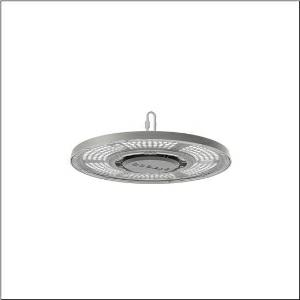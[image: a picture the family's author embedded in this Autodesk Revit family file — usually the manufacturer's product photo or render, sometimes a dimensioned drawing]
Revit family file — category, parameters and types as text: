
# Revit family: highbay_31-s_51hc42da4fmb
name_source: partatom
category: Lighting Fixtures
units: mm (PartAtom-declared; Revit-internal decimal feet)

## family parameters
Cut with Voids When Loaded = No
Host = Face
Light Source = No
Part Type = Normal
Room Calculation Point = No
Round Connector Dimension = Use Diameter
Shared = No

## types (1)
- Highbay 31-S (1 x LED, 14000 lm, 94 W, 4000K)
    Apparent Load = 94 VA
    CIE Flux Codes = 77 99 100 100 100
    Color Rendering = 80
    Color Temperature = 4000K
    Default Elevation = 1800 mm
    Description = Highbay 31-S, high bay luminaire, primary light control with lens, of PC, primary optical cover: cover panel, of PC, transparent, light emission: direct distribution, primary light characteristic: rotationally symmetric, installation type: suspended mounting, surface-mounted, LED, rated luminous flux: 14.000lm, luminous efficacy: 150lm/W, light colour: 840, colour temperature: 4000K, control gear: DALI 2, with cable, 5x 1.0mm², free wire ends, mains connection: 220..240V, AC/DC, 0/50..60Hz, cable length: 1,5m, rated input power: 94W, housing, rotationally symmetric, of diecast aluminium, powder-coated, grey aluminium (RAL 9007), with hook on luminaire side, incl. screw, diameter: 339mm, protection rating (complete): IP65, insulation class (complete): insulation class I (protective earthing), certification: CE, ENEC, UKCA, protection symbol: D, impact resistance: IK08, permissible operating ambient temperature: -30..+45°C, standard: EN 60598-2-22, EN 60598, corresponds to IFS (International Featured Standards) requirements for safety and quality in the food industry, packaging unit: 1 piece
    Height = 141 mm
    Lamp = 1 x LED
    Lamp Light Flux = 14000 lm
    Lamp Power = 94 W
    Lamp count = 1
    Length = 339 mm
    Luminous efficacy = 149 lm/W
    Manufacturer = Siteco
    ModVariant = No
    Model = 51HC42DA4FMB
    Mounting Place = Ceiling
    Mounting Type = Pendant
    Number of Poles = 1
    OnlyDefault = Yes
    Power Factor = 1
    Product Name = Highbay 31-S
    Product group = high bay luminaire
    ProductGroupID = 901
    Protection Class = Protection class I
    Protection Degree = IP 65
    RLX_Detail_Level = 1
    RLX_Emergency_Light_Flux = 0 lm
    RLX_Emergency_Type = 0
    RLX_Emergency_Type_DB = No
    RlxData = <blob elided: 162409 chars, md5=86317613>
    Socket = socket
    Standby Power = 0 W
    System Light Flux = 14000 lm
    System Power = 94 W
    Type Comments = Product without accessories
    Type Image = l_1007237.jpg
    URL = http://relux.com
    VarID = ---
    Voltage = 0 V
    Weight = 0.00 kg
    Width = 0 mm  [stored 0 ft]

note: [stored X ft] marks values corroborated as IEEE doubles in the binary element streams (Revit-internal decimal feet)

## geometry (parser evidence)
native form markers: Blend x4, Sweep x10
no freeform markers — native parametric forms only
